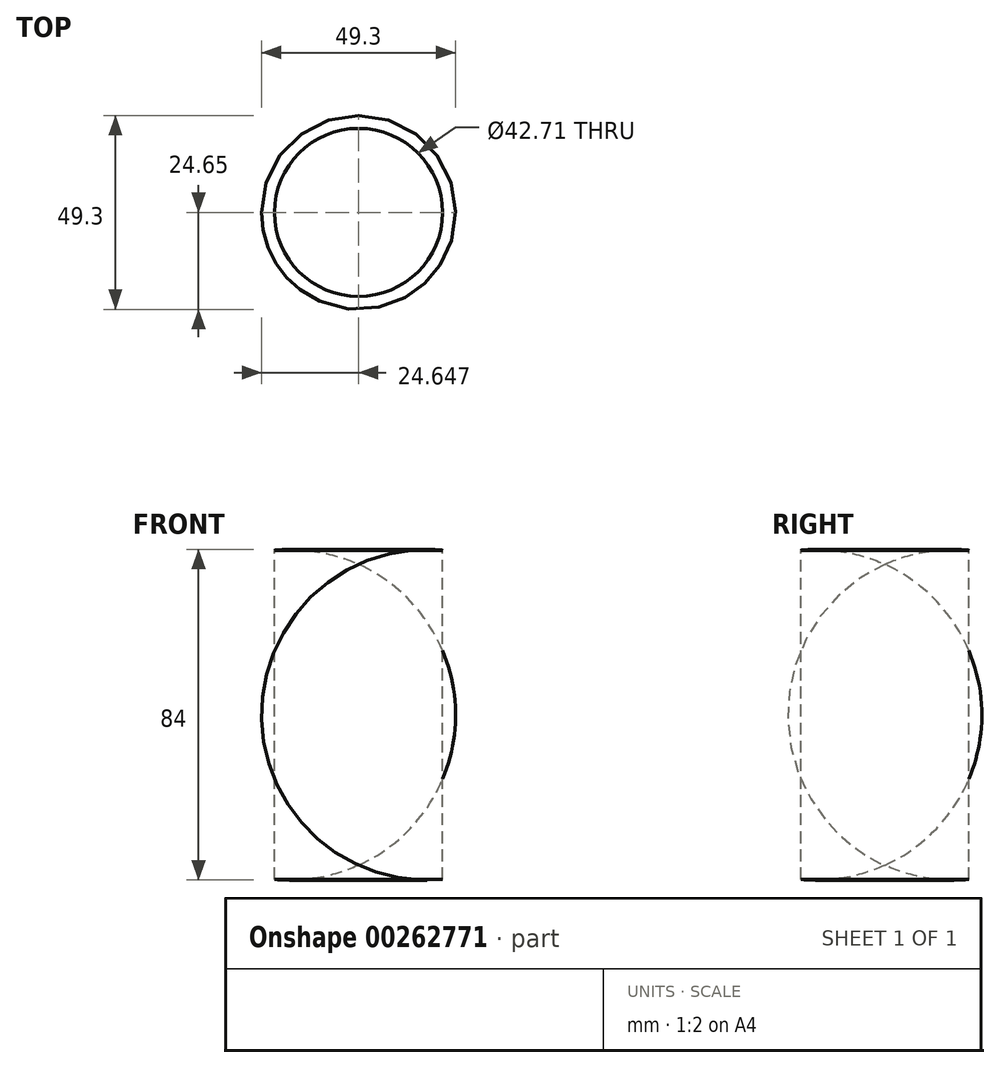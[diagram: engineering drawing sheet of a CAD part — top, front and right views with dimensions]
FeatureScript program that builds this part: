
annotation { "Feature Type Name" : "Feature", "Feature Type Description" : "" }
export const myFeature = defineFeature(function(context is Context, id is Id, definition is map)
    precondition{}
    {
        {
            var Q0;
            Q0=qCreatedBy(makeId("Front.planeOp"),FACE);
            var sketch = newSketch(context, id + "F0", { "sketchPlane" : qUnion([Q0])});
            skLineSegment(sketch, "E0", {"start": v(-39.4, 52.64) * mm, "end": v(-39.4, -29.18) * mm});
            skLineSegment(sketch, "E1", {"start": v(-18.05, 53.24) * mm, "end": v(-18.05, -30.38) * mm});
            skArc(sketch, "E2", {"start": v(-18.05, -30.38) * mm, "mid": v(19.95, 11.43) * mm, "end": v(-18.05, 53.24) * mm});
            skSolve(sketch);
        }
        {
            var Q0;
            Q0=makeQuery(id+"F0.imprint","IMPRINT",FACE,{"disambiguationData":[TD([[makeQuery(id+"F0.imprint","IMPRINT",EDGE,{"derivedFrom":sQuery(id+"F0.wireOp",EDGE,"E1")}),1.0]])]});
            var Q1;
            Q1=sQuery(id+"F0.wireOp",EDGE,"E0");
            revolve(context, id + "F1", {"entities" : qUnion([Q0]), "axis" : qUnion([Q1]), "revolveType" : RevolveType.FULL});
        }
    });
